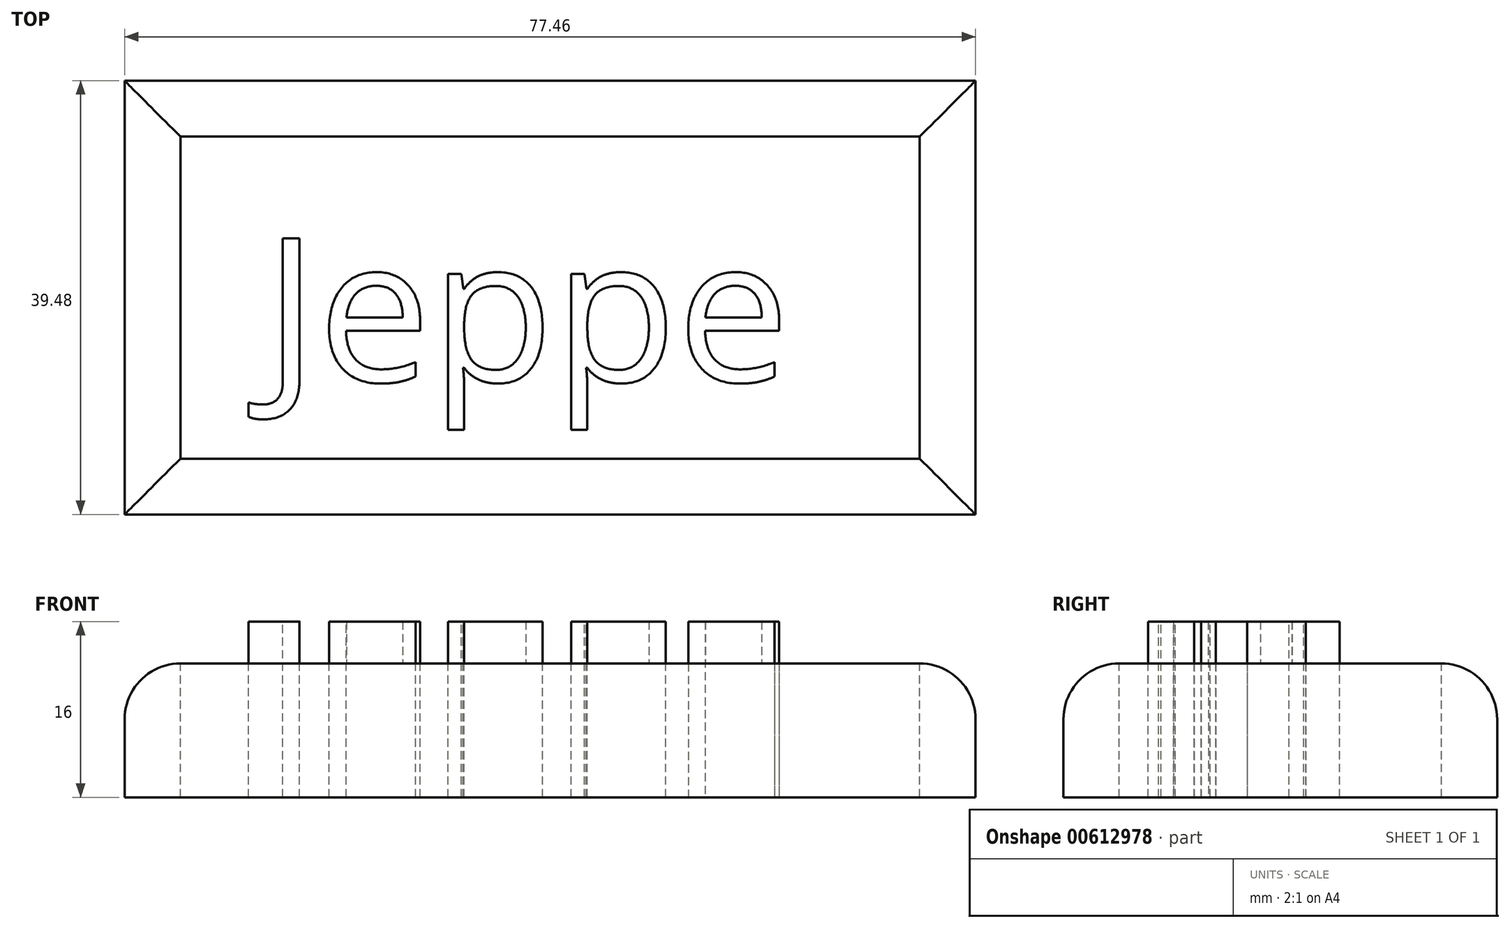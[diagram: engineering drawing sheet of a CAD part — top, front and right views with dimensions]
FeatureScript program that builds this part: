
annotation { "Feature Type Name" : "Feature", "Feature Type Description" : "" }
export const myFeature = defineFeature(function(context is Context, id is Id, definition is map)
    precondition{}
    {
        {
            var Q0;
            Q0=qCreatedBy(makeId("Top.planeOp"),FACE);
            var sketch = newSketch(context, id + "F0", { "sketchPlane" : qUnion([Q0])});
            skLineSegment(sketch, "E0.bottom", {"start": v(-34.18, 14.22) * mm, "end": v(43.28, 14.22) * mm});
            skLineSegment(sketch, "E0.top", {"start": v(-34.18, -25.26) * mm, "end": v(43.28, -25.26) * mm});
            skLineSegment(sketch, "E0.left", {"start": v(-34.18, 14.22) * mm, "end": v(-34.18, -25.26) * mm});
            skLineSegment(sketch, "E0.right", {"start": v(43.28, 14.22) * mm, "end": v(43.28, -25.26) * mm});
            skSolve(sketch);
        }
        {
            var Q0;
            Q0 = qSketchRegion(id + "F0", true);
            extrude(context, id + "F1", {"entities" : qUnion([Q0]), "depth" : 12.2 * mm, "offsetDistance" : 25.4 * mm});
        }
        {
            var Q0;
            Q0=makeQuery(id+"F1.opExtrude","CAP_EDGE",EDGE,{"disambiguationData":[OSD([sQuery(id+"F0.wireOp",EDGE,"E0.top")])],"isStart":false});
            var Q1;
            Q1=makeQuery(id+"F1.opExtrude","CAP_EDGE",EDGE,{"disambiguationData":[OSD([sQuery(id+"F0.wireOp",EDGE,"E0.bottom")])],"isStart":false});
            var Q2;
            Q2=makeQuery(id+"F1.opExtrude","CAP_EDGE",EDGE,{"disambiguationData":[OSD([sQuery(id+"F0.wireOp",EDGE,"E0.right")])],"isStart":false});
            var Q3;
            Q3=makeQuery(id+"F1.opExtrude","CAP_EDGE",EDGE,{"disambiguationData":[OSD([sQuery(id+"F0.wireOp",EDGE,"E0.left")])],"isStart":false});
            fillet(context, id + "F2", {"entities" : qUnion([Q0, Q1, Q2, Q3]), "radius" : 5.08 * mm, "tangentPropagation" : true, "allowEdgeOverflow" : false});
        }
        {
            var Q0;
            Q0=makeQuery(id+"F1.opExtrude","CAP_FACE",FACE,{"disambiguationData":[OSD([sQuery(id+"F0.wireOp",EDGE,"E0.bottom"),sQuery(id+"F0.wireOp",EDGE,"E0.top"),sQuery(id+"F0.wireOp",EDGE,"E0.left"),sQuery(id+"F0.wireOp",EDGE,"E0.right")])],"isStart":false});
            var sketch = newSketch(context, id + "F3", { "sketchPlane" : qUnion([Q0])});
            skText(sketch, "E1", { "text": "Jeppe", "fontName": "OpenSans-Regular.ttf"});
            const initialGuessF3  = {"E1": [-0.02147, -0.01317, 1, 0, 0.01317]};
            skSetInitialGuess(sketch, initialGuessF3);
            skSolve(sketch);
        }
        {
            var Q0;
            Q0 = qSketchRegion(id + "F3", true);
            extrude(context, id + "F4", {"entities" : qUnion([Q0]), "operationType" : NewBodyOperationType.ADD, "depth" : 3.8 * mm, "offsetDistance" : 25.4 * mm});
        }
        {
            var Q0;
            Q0=qCreatedBy(makeId("Right.planeOp"),FACE);
            var sketch = newSketch(context, id + "F5", { "sketchPlane" : qUnion([Q0])});
            skSolve(sketch);
        }
        {
            var Q0;
            Q0 = qSketchRegion(id + "F5", true);
            var Q1;
            {var subQ0=sQuery(id+"F0.wireOp",EDGE,"E0.bottom");var subQ1=sQuery(id+"F0.wireOp",EDGE,"E0.top");var subQ2=sQuery(id+"F0.wireOp",EDGE,"E0.left");var subQ3=sQuery(id+"F0.wireOp",EDGE,"E0.right");Q1=makeQuery(id+"F4.boolean.opBoolean","SPLIT",FACE,{"disambiguationData":[TD([makeQuery(id+"F2.opFillet","BLEND_FACE",FACE,{"disambiguationData":[OSD([subQ0])]})])],"derivedFrom":makeQuery(id+"F1.opExtrude","CAP_FACE",FACE,{"disambiguationData":[OSD([subQ0,subQ1,subQ2,subQ3])],"isStart":false})});}
            extrude(context, id + "F6", {"entities" : qUnion([Q0, Q1]), "operationType" : NewBodyOperationType.REMOVE, "oppositeDirection" : true, "depth" : 25.4 * mm, "offsetDistance" : 25.4 * mm});
        }
    });
